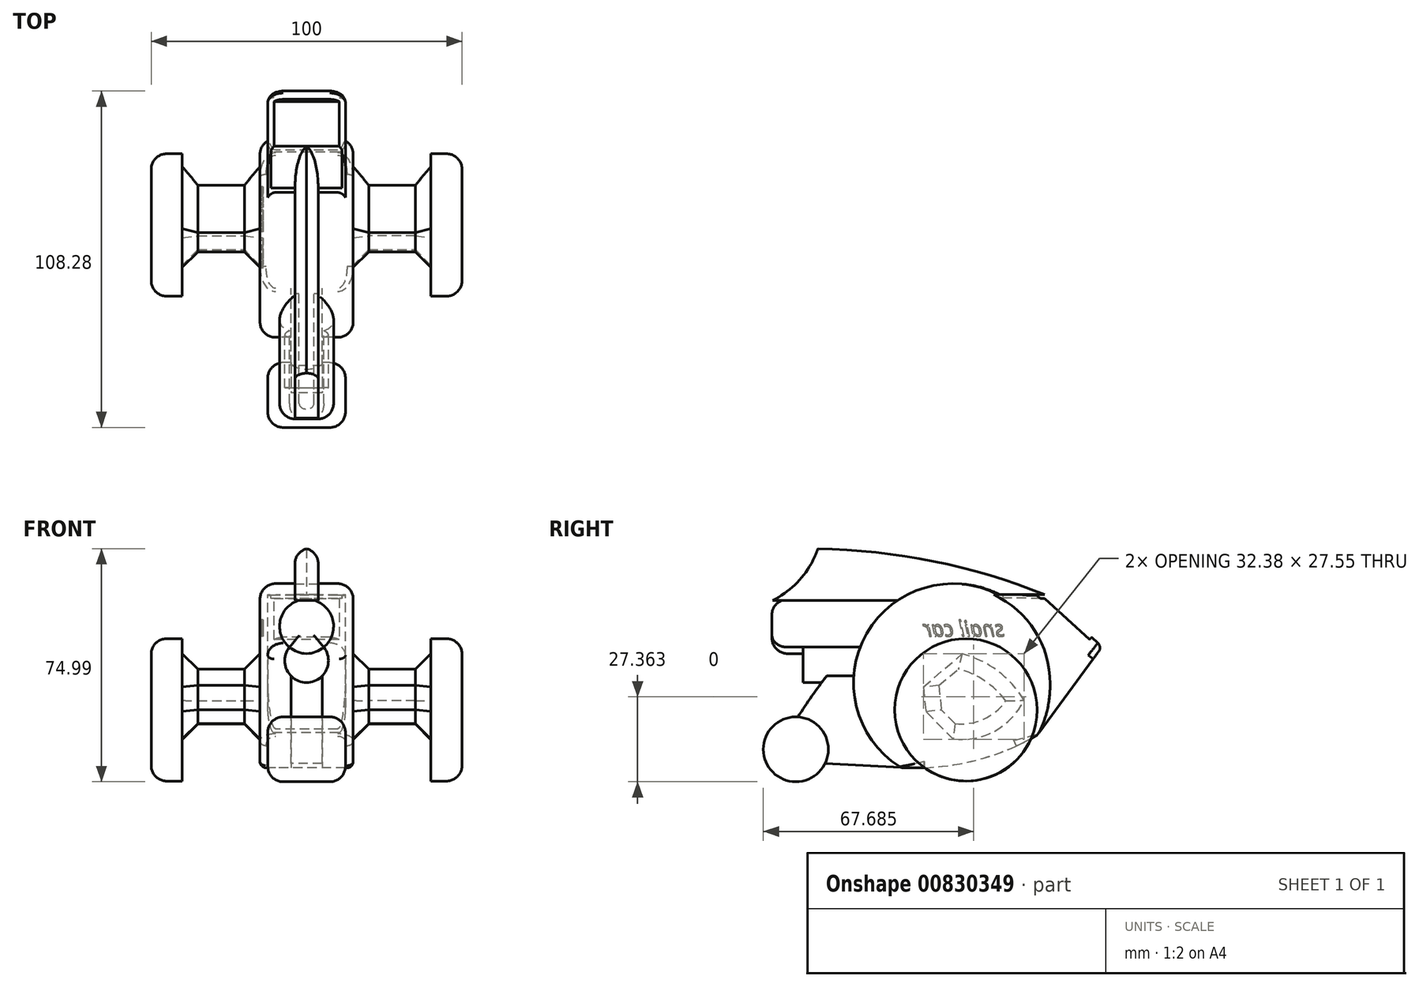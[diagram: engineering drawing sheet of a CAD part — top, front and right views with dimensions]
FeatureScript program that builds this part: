
annotation { "Feature Type Name" : "Feature", "Feature Type Description" : "" }
export const myFeature = defineFeature(function(context is Context, id is Id, definition is map)
    precondition{}
    {
        {
            var Q0;
            Q0=qCreatedBy(makeId("Right.planeOp"),FACE);
            var sketch = newSketch(context, id + "F0", { "sketchPlane" : qUnion([Q0])});
            skArc(sketch, "E0", {"start": v(27.13, -16.86) * mm, "mid": v(-7.37, 31.08) * mm, "end": v(-16.68, -27.24) * mm});
            skArc(sketch, "E1", {"start": v(-23.25, 21.91) * mm, "mid": v(-42.41, -0.2) * mm, "end": v(-58.01, -24.96) * mm});
            skLineSegment(sketch, "E2", {"start": v(-58.01, -24.96) * mm, "end": v(-16.68, -27.24) * mm});
            skArc(sketch, "E3", {"start": v(-16.68, -27.24) * mm, "mid": v(5.98, -25.23) * mm, "end": v(27.13, -16.86) * mm});
            skSolve(sketch);
        }
        {
            var Q0;
            {var subQ0=sQuery(id+"F0.wireOp",EDGE,"E2");var subQ1=sQuery(id+"F0.wireOp",EDGE,"E0");var subQ2=makeQuery(id+"F0.imprint","INTERSECT",VERTEX,{"disambiguationData":[OD(0.0)],"derivedFrom":[subQ1,subQ0]});Q0=makeQuery(id+"F0.imprint","IMPRINT",FACE,{"disambiguationData":[TD([[makeQuery(id+"F0.imprint","IMPRINT",EDGE,{"disambiguationData":[TD([[subQ2,1.0]])],"derivedFrom":subQ1}),1.0]])]});}
            var Q1;
            {var subQ0=sQuery(id+"F0.wireOp",EDGE,"E0");var subQ1=makeQuery(id+"F0.imprint","INTERSECT",VERTEX,{"derivedFrom":[subQ0,sQuery(id+"F0.wireOp",EDGE,"E1")]});Q1=makeQuery(id+"F0.imprint","IMPRINT",FACE,{"disambiguationData":[TD([[makeQuery(id+"F0.imprint","IMPRINT",EDGE,{"disambiguationData":[TD([[subQ1,-1.0]])],"derivedFrom":subQ0}),1.0]])]});}
            extrude(context, id + "F1", {"entities" : qUnion([Q0, Q1]), "endBound" : BoundingType.SYMMETRIC, "depth" : 30 * mm, "offsetDistance" : 25.4 * mm});
        }
        {
            var Q0;
            {var subQ0=sQuery(id+"F0.wireOp",EDGE,"E1");Q0=makeQuery(id+"F0.imprint","IMPRINT",FACE,{"disambiguationData":[TD([[makeQuery(id+"F0.imprint","IMPRINT",EDGE,{"derivedFrom":subQ0}),1.0]])]});}
            extrude(context, id + "F2", {"entities" : qUnion([Q0]), "operationType" : NewBodyOperationType.ADD, "endBound" : BoundingType.SYMMETRIC, "depth" : 10 * mm, "offsetDistance" : 25 * mm});
        }
        {
            var Q0;
            Q0=qCreatedBy(makeId("Right.planeOp"),FACE);
            var sketch = newSketch(context, id + "F3", { "sketchPlane" : qUnion([Q0])});
            skCircle(sketch, "E4", {"center": v(-50.5, -21.36) * mm, "radius": 10.45 * mm});
            skSolve(sketch);
        }
        {
            var Q0;
            Q0 = qSketchRegion(id + "F3", true);
            extrude(context, id + "F4", {"entities" : qUnion([Q0]), "operationType" : NewBodyOperationType.ADD, "endBound" : BoundingType.SYMMETRIC, "depth" : 25 * mm, "offsetDistance" : 25 * mm});
        }
        {
            var Q0;
            Q0=qCreatedBy(makeId("Right.planeOp"),FACE);
            var sketch = newSketch(context, id + "F5", { "sketchPlane" : qUnion([Q0])});
            skArc(sketch, "E5", {"start": v(27.7, -16.05) * mm, "mid": v(29.72, 9.05) * mm, "end": v(13.59, 28.38) * mm});
            skLineSegment(sketch, "E6", {"start": v(48, 11.6) * mm, "end": v(27.7, -16.05) * mm});
            skLineSegment(sketch, "E7", {"start": v(48, 11.6) * mm, "end": v(29.96, 28.16) * mm});
            skLineSegment(sketch, "E8", {"start": v(29.96, 28.16) * mm, "end": v(13.59, 28.38) * mm});
            skSolve(sketch);
        }
        {
            var Q0;
            Q0 = qSketchRegion(id + "F5", true);
            extrude(context, id + "F6", {"entities" : qUnion([Q0]), "operationType" : NewBodyOperationType.ADD, "endBound" : BoundingType.SYMMETRIC, "depth" : 25 * mm, "offsetDistance" : 25 * mm});
        }
        {
            var Q0;
            Q0=makeQuery(id+"F6.opExtrude","SWEPT_FACE",FACE,{"disambiguationData":[OSD([sQuery(id+"F5.wireOp",EDGE,"E7")])]});
            var sketch = newSketch(context, id + "F7", { "sketchPlane" : qUnion([Q0])});
            skLineSegment(sketch, "E9.bottom", {"start": v(11.68, 3.04) * mm, "end": v(-11.45, 3.04) * mm});
            skLineSegment(sketch, "E9.top", {"start": v(11.68, 22.96) * mm, "end": v(-11.45, 22.96) * mm});
            skLineSegment(sketch, "E9.left", {"start": v(11.68, 3.04) * mm, "end": v(11.68, 22.96) * mm});
            skLineSegment(sketch, "E9.right", {"start": v(-11.45, 3.04) * mm, "end": v(-11.45, 22.96) * mm});
            skSolve(sketch);
        }
        {
            var Q0;
            Q0 = qSketchRegion(id + "F7", true);
            extrude(context, id + "F8", {"entities" : qUnion([Q0]), "operationType" : NewBodyOperationType.REMOVE, "oppositeDirection" : true, "depth" : 1 * mm, "offsetDistance" : 25 * mm});
        }
        {
            var Q0;
            Q0=makeQuery(id+"F6.opExtrude","SWEPT_FACE",FACE,{"disambiguationData":[OSD([sQuery(id+"F5.wireOp",EDGE,"E8")])]});
            var sketch = newSketch(context, id + "F9", { "sketchPlane" : qUnion([Q0])});
            skLineSegment(sketch, "E10.bottom", {"start": v(-11.45, 29.59) * mm, "end": v(11.68, 29.59) * mm});
            skLineSegment(sketch, "E10.top", {"start": v(-11.45, 15.8) * mm, "end": v(11.68, 15.8) * mm});
            skLineSegment(sketch, "E10.left", {"start": v(-11.45, 29.59) * mm, "end": v(-11.45, 15.8) * mm});
            skLineSegment(sketch, "E10.right", {"start": v(11.68, 29.59) * mm, "end": v(11.68, 15.8) * mm});
            skSolve(sketch);
        }
        {
            var Q0;
            Q0 = qSketchRegion(id + "F9", true);
            extrude(context, id + "F10", {"entities" : qUnion([Q0]), "operationType" : NewBodyOperationType.REMOVE, "oppositeDirection" : true, "depth" : 1 * mm, "offsetDistance" : 25 * mm});
        }
        {
            var Q0;
            Q0=qCreatedBy(makeId("Front.planeOp"),FACE);
            cPlane(context, id + "F11", {"entities" : qUnion([Q0]), "cplaneType" : CPlaneType.OFFSET, "offset" : 23.2 * mm, "width" : 150 * mm, "height" : 150 * mm});
        }
        {
            var Q0;
            Q0=qCreatedBy(id+"F11.planeOp",FACE);
            var sketch = newSketch(context, id + "F12", { "sketchPlane" : qUnion([Q0])});
            skCircle(sketch, "E11", {"center": v(0, 18.2) * mm, "radius": 8.68 * mm});
            skCircle(sketch, "E12", {"center": v(0, 7.16) * mm, "radius": 7.03 * mm});
            skSolve(sketch);
        }
        {
            var Q0;
            Q0 = qSketchRegion(id + "F12", true);
            var Q1;
            Q1=sQuery(id+"F12.wireOp",EDGE,"E11");
            extrude(context, id + "F13", {"entities" : qUnion([Q0]), "operationType" : NewBodyOperationType.ADD, "surfaceOperationType" : NewSurfaceOperationType.ADD, "surfaceEntities" : qUnion([Q1]), "endBound" : BoundingType.SYMMETRIC, "depth" : 70 * mm, "offsetDistance" : 25 * mm});
        }
        {
            var Q0;
            Q0=makeQuery(id+"F13.opExtrude","CAP_FACE",FACE,{"disambiguationData":[OSD([sQuery(id+"F12.wireOp",EDGE,"E11"),sQuery(id+"F12.wireOp",EDGE,"E12")])],"isStart":false});
            var sketch = newSketch(context, id + "F14", { "sketchPlane" : qUnion([Q0])});
            skArc(sketch, "E13", {"start": v(-5.52, 11.5) * mm, "mid": v(0, 9.44) * mm, "end": v(5.52, 11.5) * mm});
            skArc(sketch, "E14", {"start": v(-5.52, 11.5) * mm, "mid": v(0, 0.07) * mm, "end": v(5.52, 11.5) * mm});
            skSolve(sketch);
        }
        {
            var Q0;
            Q0 = qSketchRegion(id + "F14", true);
            extrude(context, id + "F15", {"entities" : qUnion([Q0]), "operationType" : NewBodyOperationType.REMOVE, "oppositeDirection" : true, "depth" : 10 * mm, "offsetDistance" : 25 * mm});
        }
        {
            var Q0;
            Q0=makeQuery(id+"F1.opExtrude","CAP_FACE",FACE,{"disambiguationData":[OSD([sQuery(id+"F0.wireOp",EDGE,"E0")])],"isStart":false});
            var sketch = newSketch(context, id + "F16", { "sketchPlane" : qUnion([Q0])});
            skArc(sketch, "E15", {"start": v(17.03, -5.78) * mm, "mid": v(7.3, 2.4) * mm, "end": v(-5.06, 5.37) * mm});
            skArc(sketch, "E16", {"start": v(-3.4, -12.18) * mm, "mid": v(7.9, -12.44) * mm, "end": v(17.03, -5.78) * mm});
            skLineSegment(sketch, "E17", {"start": v(-5.06, 5.37) * mm, "end": v(-3.4, -12.18) * mm});
            skSolve(sketch);
        }
        {
            var Q0;
            Q0 = qSketchRegion(id + "F16", true);
            extrude(context, id + "F17", {"entities" : qUnion([Q0]), "operationType" : NewBodyOperationType.ADD, "depth" : 25 * mm, "offsetDistance" : 25 * mm});
        }
        {
            var Q0;
            Q0=makeQuery(id+"F17.opExtrude","CAP_FACE",FACE,{"disambiguationData":[OSD([sQuery(id+"F16.wireOp",EDGE,"E15"),sQuery(id+"F16.wireOp",EDGE,"E16"),sQuery(id+"F16.wireOp",EDGE,"E17")])],"isStart":false});
            var sketch = newSketch(context, id + "F18", { "sketchPlane" : qUnion([Q0])});
            skCircle(sketch, "E18", {"center": v(4.23, -8.67) * mm, "radius": 22.91 * mm});
            skSolve(sketch);
        }
        {
            var Q0;
            Q0 = qSketchRegion(id + "F18", true);
            extrude(context, id + "F19", {"entities" : qUnion([Q0]), "operationType" : NewBodyOperationType.ADD, "depth" : 10 * mm, "offsetDistance" : 25 * mm});
        }
        {
            var Q0;
            Q0=makeQuery(id+"F1.opExtrude","SWEPT_BODY",BODY,{"disambiguationData":[OSD([sQuery(id+"F0.wireOp",EDGE,"E0")])]});
            var Q1;
            Q1=qCreatedBy(makeId("Right.planeOp"),FACE);
            mirror(context, id + "F20", {"entities" : qUnion([Q0]), "mirrorPlane" : qUnion([Q1])});
        }
        {
            var Q0;
            Q0=qCreatedBy(makeId("Right.planeOp"),FACE);
            var sketch = newSketch(context, id + "F21", { "sketchPlane" : qUnion([Q0])});
            skArc(sketch, "E19", {"start": v(29.92, 28.45) * mm, "mid": v(-6.03, 39.24) * mm, "end": v(-43.35, 43.34) * mm});
            skArc(sketch, "E20", {"start": v(-57.95, 26.55) * mm, "mid": v(-48.98, 33.5) * mm, "end": v(-43.35, 43.34) * mm});
            skLineSegment(sketch, "E21", {"start": v(29.92, 28.45) * mm, "end": v(15.03, 28.45) * mm});
            skArc(sketch, "E22", {"start": v(15.03, 28.45) * mm, "mid": v(-1.28, 31.84) * mm, "end": v(-17.08, 26.55) * mm});
            skLineSegment(sketch, "E23", {"start": v(-17.08, 26.55) * mm, "end": v(-57.95, 26.55) * mm});
            skSolve(sketch);
        }
        {
            var Q0;
            Q0 = qSketchRegion(id + "F21", true);
            extrude(context, id + "F22", {"entities" : qUnion([Q0]), "operationType" : NewBodyOperationType.ADD, "endBound" : BoundingType.SYMMETRIC, "depth" : 7.5 * mm, "offsetDistance" : 25 * mm});
        }
        {
            var Q0;
            Q0=makeQuery(id+"F22.opExtrude","CAP_EDGE",EDGE,{"disambiguationData":[OSD([sQuery(id+"F21.wireOp",EDGE,"E19")])],"isStart":false});
            var Q1;
            Q1=makeQuery(id+"F22.opExtrude","CAP_EDGE",EDGE,{"disambiguationData":[OSD([sQuery(id+"F21.wireOp",EDGE,"E19")])],"isStart":true});
            var Q2;
            Q2=makeQuery(id+"F1.opExtrude","CAP_EDGE",EDGE,{"disambiguationData":[OSD([sQuery(id+"F0.wireOp",EDGE,"E0")])],"isStart":true});
            var Q3;
            Q3=makeQuery(id+"F1.opExtrude","CAP_EDGE",EDGE,{"disambiguationData":[OSD([sQuery(id+"F0.wireOp",EDGE,"E0")])],"isStart":false});
            var Q4;
            Q4=makeQuery(id+"F19.opExtrude","CAP_EDGE",EDGE,{"disambiguationData":[OSD([sQuery(id+"F18.wireOp",EDGE,"E18")])],"isStart":false});
            var Q5;
            Q5=makeQuery(id+"F20.opPattern","COPY",EDGE,{"derivedFrom":makeQuery(id+"F19.opExtrude","CAP_EDGE",EDGE,{"disambiguationData":[OSD([sQuery(id+"F18.wireOp",EDGE,"E18")])],"isStart":false}),"instanceName":"1"});
            var Q6;
            Q6=makeQuery(id+"F4.opExtrude","CAP_EDGE",EDGE,{"disambiguationData":[OSD([sQuery(id+"F3.wireOp",EDGE,"E4")])],"isStart":true});
            var Q7;
            Q7=makeQuery(id+"F4.opExtrude","CAP_EDGE",EDGE,{"disambiguationData":[OSD([sQuery(id+"F3.wireOp",EDGE,"E4")])],"isStart":false});
            var Q8;
            Q8=makeQuery(id+"F6.opExtrude","CAP_EDGE",EDGE,{"disambiguationData":[OSD([sQuery(id+"F5.wireOp",EDGE,"E7")])],"isStart":true});
            var Q9;
            Q9=makeQuery(id+"F6.opExtrude","CAP_EDGE",EDGE,{"disambiguationData":[OSD([sQuery(id+"F5.wireOp",EDGE,"E7")])],"isStart":false});
            var Q10;
            Q10=makeQuery(id+"F3y0kcKC9sblVyD_1.boolean.opBoolean","COPY",EDGE,{"derivedFrom":makeQuery(id+"F3y0kcKC9sblVyD_1.opExtrude","CAP_EDGE",EDGE,{"disambiguationData":[OSD([sQuery(id+"FJdVXqIRoFJi4PQ_1.wireOp",EDGE,"iynLRI7J-clmP-pWwm-Ukjn-tPNC3Za7MZ2C")])],"isStart":true})});
            var Q11;
            Q11=makeQuery(id+"F13.opExtrude","CAP_EDGE",EDGE,{"disambiguationData":[OSD([sQuery(id+"F12.wireOp",EDGE,"E11")])],"isStart":false});
            var Q12;
            Q12=makeQuery(id+"F15.boolean.opBoolean","COPY",EDGE,{"derivedFrom":makeQuery(id+"F15.opExtrude","CAP_EDGE",EDGE,{"disambiguationData":[OSD([sQuery(id+"F14.wireOp",EDGE,"E13")])],"isStart":true})});
            fillet(context, id + "F23", {"entities" : qUnion([Q0, Q1, Q2, Q3, Q4, Q5, Q6, Q7, Q8, Q9, Q10, Q11, Q12]), "radius" : 5 * mm, "tangentPropagation" : true, "allowEdgeOverflow" : false});
        }
        {
            var Q0;
            Q0=makeQuery(id+"F20.opPattern","COPY",FACE,{"derivedFrom":makeQuery(id+"F17.opExtrude","SWEPT_FACE",FACE,{"disambiguationData":[OSD([sQuery(id+"F16.wireOp",EDGE,"E17")])]}),"instanceName":"1"});
            var Q1;
            Q1=makeQuery(id+"F17.opExtrude","SWEPT_FACE",FACE,{"disambiguationData":[OSD([sQuery(id+"F16.wireOp",EDGE,"E17")])]});
            chamfer(context, id + "F24", {"entities" : qUnion([Q0, Q1]), "width" : 5 * mm, "tangentPropagation" : true});
        }
        {
            var Q0;
            Q0=makeQuery(id+"F1.opExtrude","CAP_FACE",FACE,{"disambiguationData":[OSD([sQuery(id+"F0.wireOp",EDGE,"E0"),sQuery(id+"F0.wireOp",EDGE,"E3")])],"isStart":true});
            var sketch = newSketch(context, id + "F25", { "sketchPlane" : qUnion([Q0])});
            skText(sketch, "E24", { "text": "snail car", "fontName": "OpenSans-Italic.ttf"});
            const initialGuessF25  = {"E24": [-0.01647, 0.015, 1, 0, 0.00498]};
            skSetInitialGuess(sketch, initialGuessF25);
            skSolve(sketch);
        }
        {
            var Q0;
            Q0 = qSketchRegion(id + "F25", true);
            extrude(context, id + "F26", {"entities" : qUnion([Q0]), "operationType" : NewBodyOperationType.REMOVE, "oppositeDirection" : true, "depth" : 1 * mm, "offsetDistance" : 25 * mm});
        }
        {
            var Q0;
            Q0=makeQuery(id+"F6.opExtrude","SWEPT_EDGE",EDGE,{"disambiguationData":[OSD([sQuery(id+"F5.wireOp",EDGE,"E6"),sQuery(id+"F5.wireOp",EDGE,"E7")])]});
            var Q1;
            Q1=makeQuery(id+"F1.opExtrude","SWEPT_EDGE",EDGE,{"disambiguationData":[OSD([sQuery(id+"F0.wireOp",EDGE,"E0"),sQuery(id+"F0.wireOp",EDGE,"E3")])]});
            fillet(context, id + "F27", {"entities" : qUnion([Q0, Q1]), "radius" : 2 * mm, "tangentPropagation" : true, "allowEdgeOverflow" : false});
        }
    });
